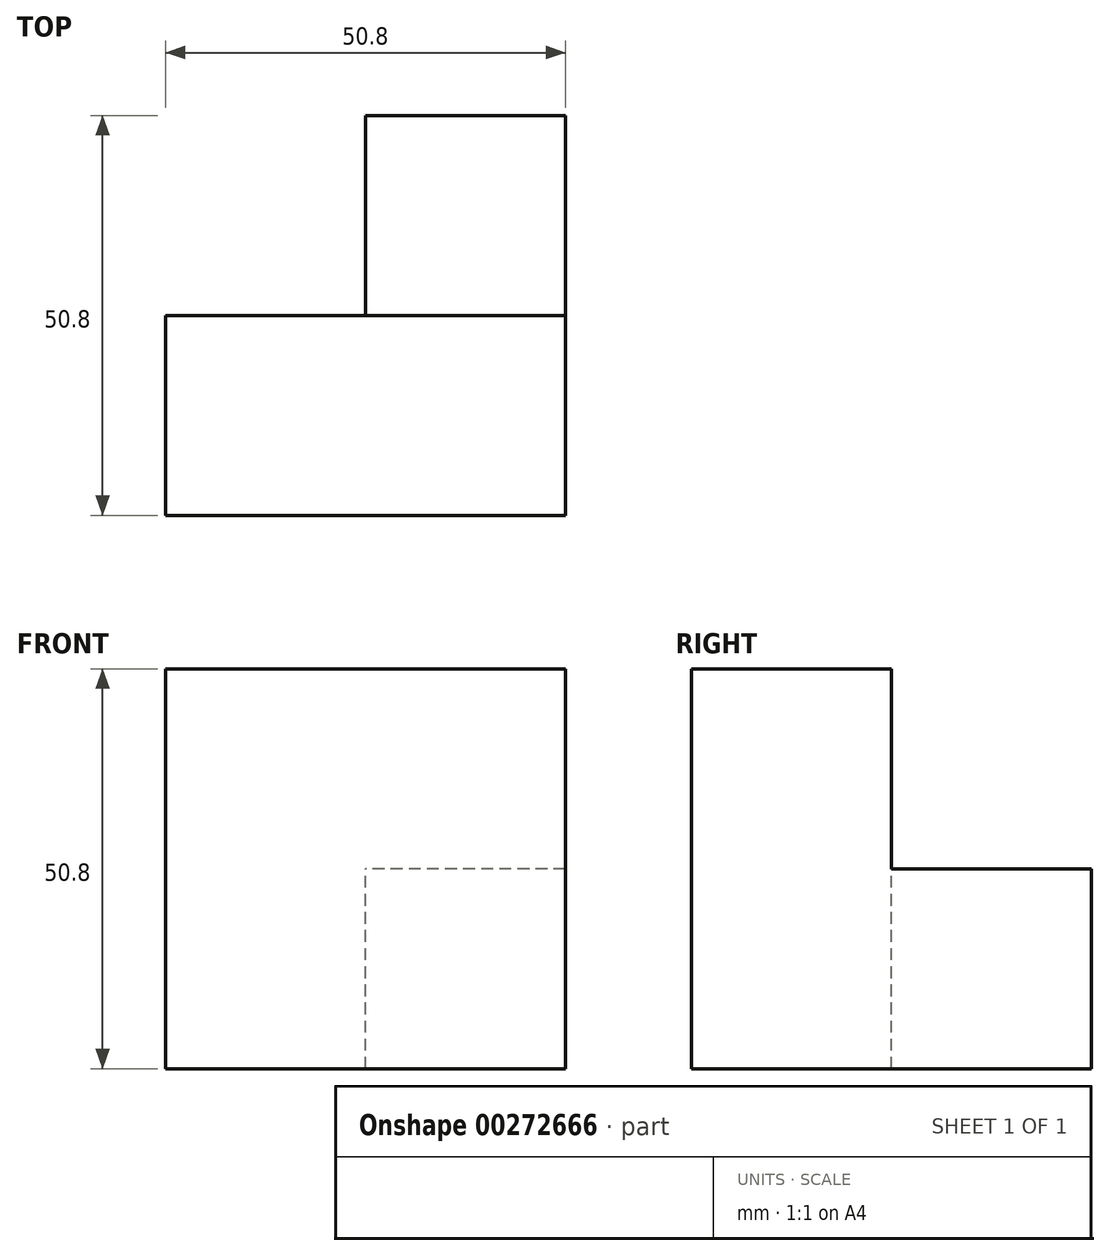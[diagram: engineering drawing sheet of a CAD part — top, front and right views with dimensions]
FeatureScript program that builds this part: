
annotation { "Feature Type Name" : "Feature", "Feature Type Description" : "" }
export const myFeature = defineFeature(function(context is Context, id is Id, definition is map)
    precondition{}
    {
        {
            var Q0;
            Q0=qCreatedBy(makeId("Front.planeOp"),FACE);
            var sketch = newSketch(context, id + "F0", { "sketchPlane" : qUnion([Q0])});
            skLineSegment(sketch, "E0.bottom", {"start": v(0, 0) * mm, "end": v(-50.8, 0) * mm});
            skLineSegment(sketch, "E0.top", {"start": v(0, 50.8) * mm, "end": v(-50.8, 50.8) * mm});
            skLineSegment(sketch, "E0.left", {"start": v(0, 0) * mm, "end": v(0, 50.8) * mm});
            skLineSegment(sketch, "E0.right", {"start": v(-50.8, 0) * mm, "end": v(-50.8, 50.8) * mm});
            skSolve(sketch);
        }
        {
            var Q0;
            Q0=makeQuery(id+"F0.imprint","IMPRINT",FACE,{"disambiguationData":[TD([[makeQuery(id+"F0.imprint","IMPRINT",EDGE,{"derivedFrom":sQuery(id+"F0.wireOp",EDGE,"E0.bottom")}),-1.0]])]});
            extrude(context, id + "F1", {"entities" : qUnion([Q0]), "depth" : 25.4 * mm});
        }
        {
            var Q0;
            Q0=makeQuery(id+"F1.opExtrude","CAP_FACE",FACE,{"disambiguationData":[OSD([sQuery(id+"F0.wireOp",EDGE,"E0.bottom"),sQuery(id+"F0.wireOp",EDGE,"E0.top"),sQuery(id+"F0.wireOp",EDGE,"E0.left"),sQuery(id+"F0.wireOp",EDGE,"E0.right")])],"isStart":true});
            var sketch = newSketch(context, id + "F2", { "sketchPlane" : qUnion([Q0])});
            skLineSegment(sketch, "E1.bottom", {"start": v(0, 0) * mm, "end": v(25.4, 0) * mm});
            skLineSegment(sketch, "E1.top", {"start": v(0, 25.4) * mm, "end": v(25.4, 25.4) * mm});
            skLineSegment(sketch, "E1.left", {"start": v(0, 0) * mm, "end": v(0, 25.4) * mm});
            skLineSegment(sketch, "E1.right", {"start": v(25.4, 0) * mm, "end": v(25.4, 25.4) * mm});
            skSolve(sketch);
        }
        {
            var Q0;
            Q0 = qSketchRegion(id + "F2", true);
            extrude(context, id + "F3", {"entities" : qUnion([Q0]), "operationType" : NewBodyOperationType.ADD, "depth" : 25.4 * mm});
        }
    });
